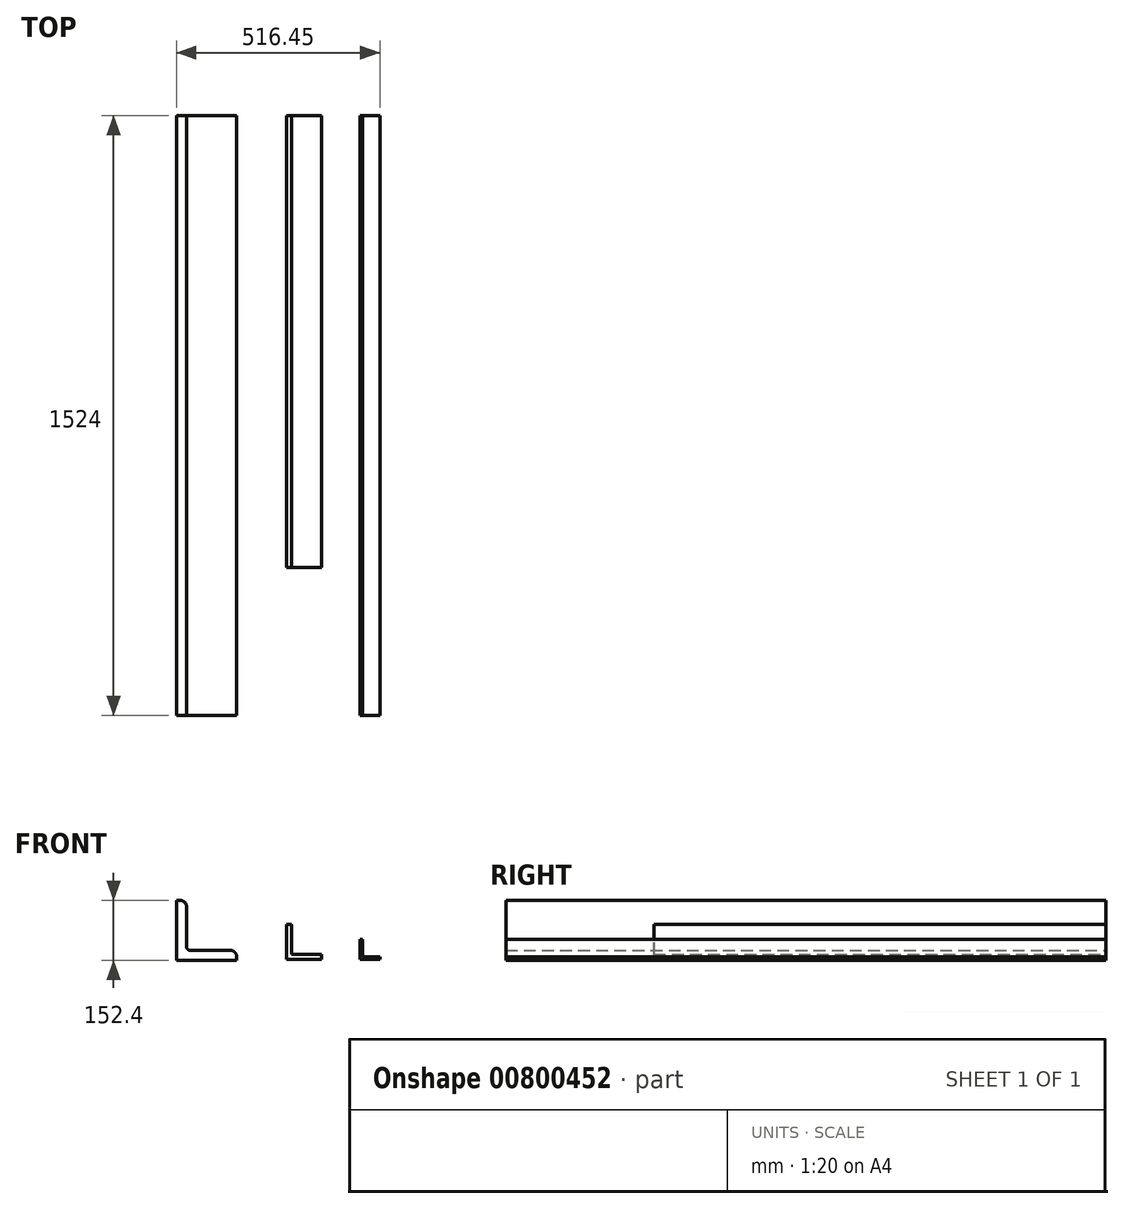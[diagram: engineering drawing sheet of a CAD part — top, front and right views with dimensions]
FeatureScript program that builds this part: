
annotation { "Feature Type Name" : "Feature", "Feature Type Description" : "" }
export const myFeature = defineFeature(function(context is Context, id is Id, definition is map)
    precondition{}
    {
        {
            var Q0;
            Q0=qCreatedBy(makeId("Front.planeOp"),FACE);
            var sketch = newSketch(context, id + "F0", { "sketchPlane" : qUnion([Q0])});
            skLineSegment(sketch, "E0", {"start": v(-53.77, 149.52) * mm, "end": v(-53.77, -2.88) * mm});
            skLineSegment(sketch, "E1", {"start": v(-53.77, -2.88) * mm, "end": v(98.63, -2.88) * mm});
            skLineSegment(sketch, "E2", {"start": v(-53.77, 149.52) * mm, "end": v(-44.24, 149.52) * mm});
            skLineSegment(sketch, "E3", {"start": v(-28.37, 133.65) * mm, "end": v(-28.37, 32.04) * mm});
            skLineSegment(sketch, "E4", {"start": v(-18.84, 22.52) * mm, "end": v(82.88, 22.52) * mm});
            skLineSegment(sketch, "E5", {"start": v(98.76, 6.44) * mm, "end": v(98.63, -2.88) * mm});
            skPoint(sketch, "E6.visualSharp", {"position": v(98.97, 22.52) * mm});
            skArc(sketch, "E6.filletArc", {"start": v(98.76, 6.44) * mm, "mid": v(94.18, 17.8) * mm, "end": v(82.88, 22.52) * mm});
            skPoint(sketch, "E7.visualSharp", {"position": v(-28.37, 149.52) * mm});
            skArc(sketch, "E7.filletArc", {"start": v(-28.37, 133.65) * mm, "mid": v(-33.02, 144.87) * mm, "end": v(-44.24, 149.52) * mm});
            skPoint(sketch, "E8.visualSharp", {"position": v(-28.37, 22.52) * mm});
            skArc(sketch, "E8.filletArc", {"start": v(-28.37, 32.04) * mm, "mid": v(-25.58, 25.3) * mm, "end": v(-18.84, 22.52) * mm});
            skSolve(sketch);
        }
        {
            var Q0;
            Q0 = qSketchRegion(id + "F0", true);
            extrude(context, id + "F1", {"entities" : qUnion([Q0]), "depth" : 1524 * mm, "offsetDistance" : 25.4 * mm});
        }
        {
            var Q0;
            Q0=qCreatedBy(makeId("Front.planeOp"),FACE);
            var sketch = newSketch(context, id + "F2", { "sketchPlane" : qUnion([Q0])});
            skLineSegment(sketch, "E9", {"start": v(226.11, 88.9) * mm, "end": v(226.11, 0) * mm});
            skLineSegment(sketch, "E10", {"start": v(226.11, 0) * mm, "end": v(315.01, 0) * mm});
            skLineSegment(sketch, "E11", {"start": v(315.01, 0) * mm, "end": v(315.01, 12.7) * mm});
            skLineSegment(sketch, "E12", {"start": v(315.01, 12.7) * mm, "end": v(238.81, 12.7) * mm});
            skLineSegment(sketch, "E13", {"start": v(238.81, 12.7) * mm, "end": v(238.81, 88.9) * mm});
            skLineSegment(sketch, "E14", {"start": v(238.81, 88.9) * mm, "end": v(226.11, 88.9) * mm});
            skSolve(sketch);
        }
        {
            var Q0;
            Q0 = qSketchRegion(id + "F2", true);
            extrude(context, id + "F3", {"entities" : qUnion([Q0]), "depth" : 1147.76 * mm, "offsetDistance" : 25.4 * mm});
        }
        {
            var Q0;
            Q0=qCreatedBy(makeId("Front.planeOp"),FACE);
            var sketch = newSketch(context, id + "F4", { "sketchPlane" : qUnion([Q0])});
            skLineSegment(sketch, "E15", {"start": v(411.88, 50.8) * mm, "end": v(411.88, 0) * mm});
            skLineSegment(sketch, "E16", {"start": v(411.88, 0) * mm, "end": v(462.68, 0) * mm});
            skLineSegment(sketch, "E17", {"start": v(462.68, 0) * mm, "end": v(462.68, 6.35) * mm});
            skLineSegment(sketch, "E18", {"start": v(462.68, 6.35) * mm, "end": v(418.23, 6.35) * mm});
            skLineSegment(sketch, "E19", {"start": v(418.23, 6.35) * mm, "end": v(418.23, 50.8) * mm});
            skLineSegment(sketch, "E20", {"start": v(418.23, 50.8) * mm, "end": v(411.88, 50.8) * mm});
            skSolve(sketch);
        }
        {
            var Q0;
            Q0 = qSketchRegion(id + "F4", true);
            extrude(context, id + "F5", {"entities" : qUnion([Q0]), "depth" : 1524 * mm, "offsetDistance" : 25.4 * mm});
        }
    });
